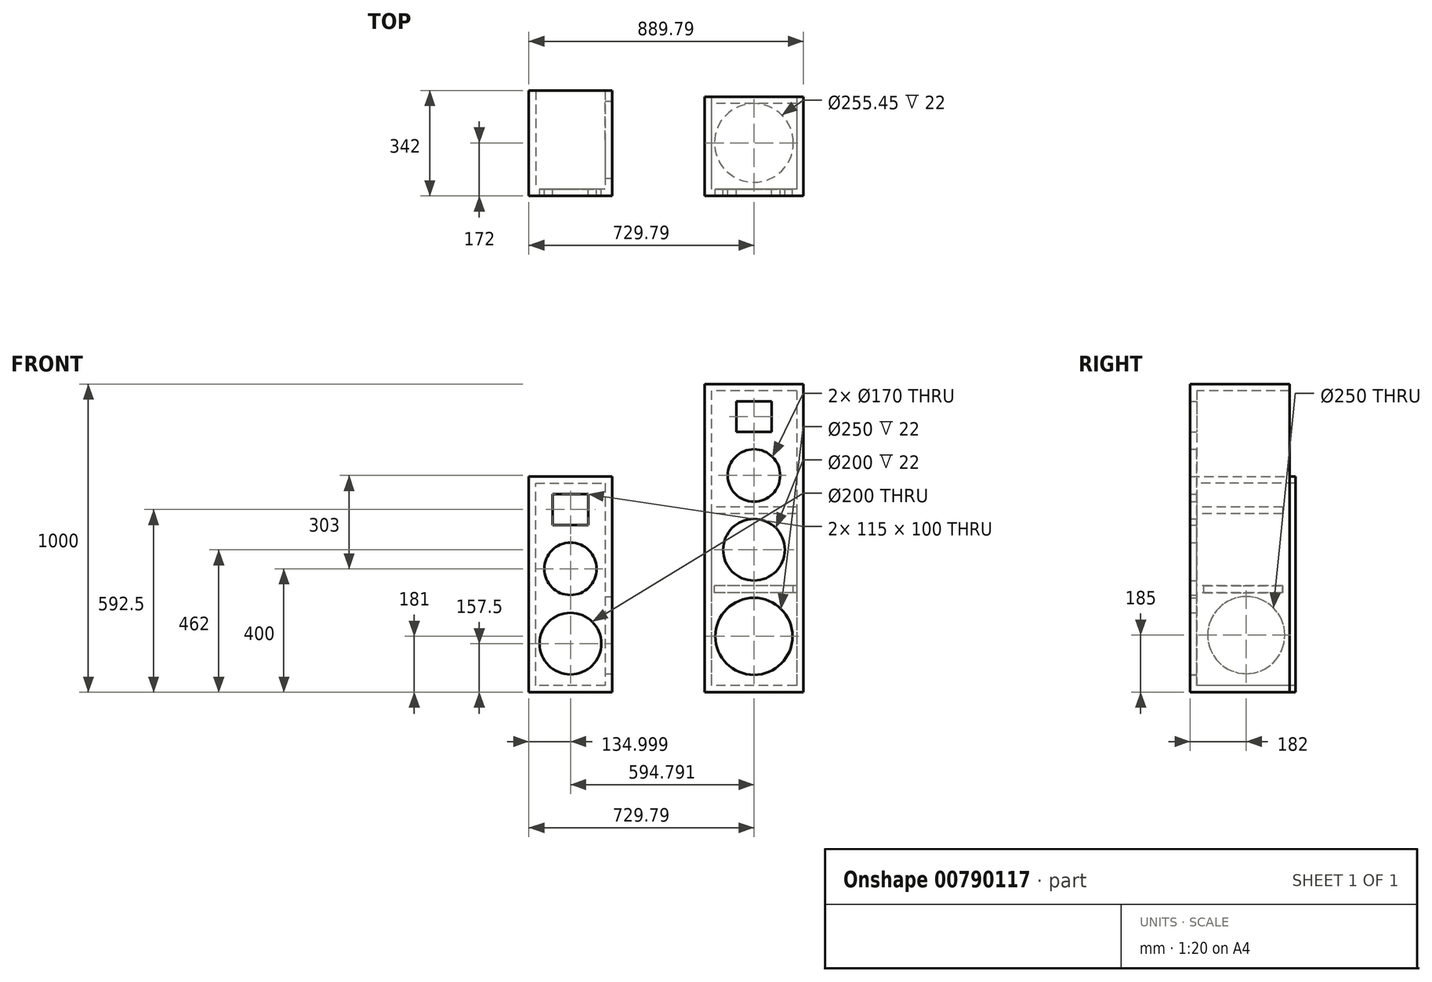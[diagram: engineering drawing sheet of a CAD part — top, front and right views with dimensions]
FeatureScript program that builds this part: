
annotation { "Feature Type Name" : "Feature", "Feature Type Description" : "" }
export const myFeature = defineFeature(function(context is Context, id is Id, definition is map)
    precondition{}
    {
        {
            var Q0;
            Q0=qCreatedBy(makeId("Front.planeOp"),FACE);
            var sketch = newSketch(context, id + "F0", { "sketchPlane" : qUnion([Q0])});
            skLineSegment(sketch, "E0.bottom", {"start": v(-160, 538) * mm, "end": v(160, 538) * mm});
            skLineSegment(sketch, "E0.top", {"start": v(-160, -462) * mm, "end": v(160, -462) * mm});
            skLineSegment(sketch, "E0.left", {"start": v(-160, 538) * mm, "end": v(-160, -462) * mm});
            skLineSegment(sketch, "E0.right", {"start": v(160, 538) * mm, "end": v(160, -462) * mm});
            skCircle(sketch, "E1", {"center": v(0, -281) * mm, "radius": 125 * mm});
            skCircle(sketch, "E2", {"center": v(0, 0) * mm, "radius": 100 * mm});
            skCircle(sketch, "E3", {"center": v(0, 241) * mm, "radius": 85 * mm});
            skLineSegment(sketch, "E4.bottom", {"start": v(-57.5, 482) * mm, "end": v(57.5, 482) * mm});
            skLineSegment(sketch, "E4.top", {"start": v(-57.5, 382) * mm, "end": v(57.5, 382) * mm});
            skLineSegment(sketch, "E4.left", {"start": v(-57.5, 482) * mm, "end": v(-57.5, 382) * mm});
            skLineSegment(sketch, "E4.right", {"start": v(57.5, 482) * mm, "end": v(57.5, 382) * mm});
            skLineSegment(sketch, "E5.bottom", {"start": v(-729.8, 238) * mm, "end": v(-459.8, 238) * mm});
            skLineSegment(sketch, "E5.top", {"start": v(-729.8, -462) * mm, "end": v(-459.8, -462) * mm});
            skLineSegment(sketch, "E5.left", {"start": v(-729.8, 238) * mm, "end": v(-729.8, -462) * mm});
            skLineSegment(sketch, "E5.right", {"start": v(-459.8, 238) * mm, "end": v(-459.8, -462) * mm});
            skCircle(sketch, "E6", {"center": v(-594.8, -304.5) * mm, "radius": 100 * mm});
            skCircle(sketch, "E7", {"center": v(-594.8, -62) * mm, "radius": 85 * mm});
            skPoint(sketch, "E8", {"position": v(0, 432) * mm});
            skLineSegment(sketch, "E9.bottom", {"start": v(-652.3, 180.5) * mm, "end": v(-537.3, 180.5) * mm});
            skLineSegment(sketch, "E9.top", {"start": v(-652.3, 80.5) * mm, "end": v(-537.3, 80.5) * mm});
            skLineSegment(sketch, "E9.left", {"start": v(-652.3, 180.5) * mm, "end": v(-652.3, 80.5) * mm});
            skLineSegment(sketch, "E9.right", {"start": v(-537.3, 180.5) * mm, "end": v(-537.3, 80.5) * mm});
            skSolve(sketch);
        }
        {
            var Q0;
            Q0 = qSketchRegion(id + "F0", true);
            extrude(context, id + "F1", {"entities" : qUnion([Q0]), "depth" : 22 * mm, "offsetDistance" : 25 * mm});
        }
        {
            var Q0;
            Q0=makeQuery(id+"F1.opExtrude","CAP_FACE",FACE,{"disambiguationData":[OSD([sQuery(id+"F0.wireOp",EDGE,"E0.bottom"),sQuery(id+"F0.wireOp",EDGE,"E0.top"),sQuery(id+"F0.wireOp",EDGE,"E0.left"),sQuery(id+"F0.wireOp",EDGE,"E0.right"),sQuery(id+"F0.wireOp",EDGE,"E1"),sQuery(id+"F0.wireOp",EDGE,"E2"),sQuery(id+"F0.wireOp",EDGE,"E3"),sQuery(id+"F0.wireOp",EDGE,"E4.bottom"),sQuery(id+"F0.wireOp",EDGE,"E4.top"),sQuery(id+"F0.wireOp",EDGE,"E4.left"),sQuery(id+"F0.wireOp",EDGE,"E4.right")])],"isStart":true});
            var sketch = newSketch(context, id + "F2", { "sketchPlane" : qUnion([Q0])});
            skLineSegment(sketch, "E10.bottom", {"start": v(-138, 516) * mm, "end": v(138, 516) * mm});
            skLineSegment(sketch, "E10.top", {"start": v(-138, -440) * mm, "end": v(138, -440) * mm});
            skLineSegment(sketch, "E10.left", {"start": v(-138, 516) * mm, "end": v(-138, -440) * mm});
            skLineSegment(sketch, "E10.right", {"start": v(138, 516) * mm, "end": v(138, -440) * mm});
            skSolve(sketch);
        }
        {
            var Q0;
            Q0=qCreatedBy(makeId("Front.planeOp"),FACE);
            var sketch = newSketch(context, id + "F3", { "sketchPlane" : qUnion([Q0])});
            skLineSegment(sketch, "E11.0", {"start": v(-707.8, -440) * mm, "end": v(-707.8, 216) * mm});
            skLineSegment(sketch, "E11.1", {"start": v(-481.8, -440) * mm, "end": v(-707.8, -440) * mm});
            skLineSegment(sketch, "E11.2", {"start": v(-481.8, 216) * mm, "end": v(-481.8, -440) * mm});
            skLineSegment(sketch, "E11.3", {"start": v(-707.8, 216) * mm, "end": v(-481.8, 216) * mm});
            skSolve(sketch);
        }
        {
            var Q0;
            Q0=makeQuery(id+"F1.opExtrude","CAP_FACE",FACE,{"disambiguationData":[OSD([sQuery(id+"F0.wireOp",EDGE,"E5.bottom"),sQuery(id+"F0.wireOp",EDGE,"E5.top"),sQuery(id+"F0.wireOp",EDGE,"E5.left"),sQuery(id+"F0.wireOp",EDGE,"E5.right"),sQuery(id+"F0.wireOp",EDGE,"E6"),sQuery(id+"F0.wireOp",EDGE,"E7"),sQuery(id+"F0.wireOp",EDGE,"ergSRJjx-bGEk-UiLp-R56Z-rpadYB1vBW9F.bottom"),sQuery(id+"F0.wireOp",EDGE,"ergSRJjx-bGEk-UiLp-R56Z-rpadYB1vBW9F.top"),sQuery(id+"F0.wireOp",EDGE,"ergSRJjx-bGEk-UiLp-R56Z-rpadYB1vBW9F.left"),sQuery(id+"F0.wireOp",EDGE,"ergSRJjx-bGEk-UiLp-R56Z-rpadYB1vBW9F.right")])],"isStart":true});
            extrude(context, id + "F4", {"entities" : qUnion([Q0]), "operationType" : NewBodyOperationType.ADD, "depth" : 320 * mm, "offsetDistance" : 25 * mm});
        }
        {
            var Q0;
            Q0=makeQuery(id+"F3.imprint","IMPRINT",FACE,{"disambiguationData":[TD([[makeQuery(id+"F3.imprint","IMPRINT",EDGE,{"derivedFrom":sQuery(id+"F3.wireOp",EDGE,"E11.0")}),-1.0]])]});
            extrude(context, id + "F5", {"entities" : qUnion([Q0]), "operationType" : NewBodyOperationType.REMOVE, "oppositeDirection" : true, "depth" : 824 * mm, "offsetDistance" : 25 * mm});
        }
        {
            var Q0;
            Q0=makeQuery(id+"F2.imprint","IMPRINT",FACE,{"disambiguationData":[TD([[makeQuery(id+"F2.imprint","IMPRINT",EDGE,{"derivedFrom":sQuery(id+"F2.wireOp",EDGE,"E10.bottom")}),1.0]])]});
            extrude(context, id + "F6", {"entities" : qUnion([Q0]), "operationType" : NewBodyOperationType.ADD, "depth" : 300 * mm, "offsetDistance" : 25 * mm});
        }
        {
            var Q0;
            {var subQ0=sQuery(id+"F0.wireOp",EDGE,"E5.right");Q0=makeQuery(id+"F4.boolean.opBoolean","MERGE",FACE,{"derivedFrom":[makeQuery(id+"F1.opExtrude","SWEPT_FACE",FACE,{"disambiguationData":[OSD([subQ0])]}),makeQuery(id+"F4.opExtrude","SWEPT_FACE",FACE,{"disambiguationData":[OSD([subQ0])]})]});}
            var sketch = newSketch(context, id + "F7", { "sketchPlane" : qUnion([Q0])});
            skCircle(sketch, "E12", {"center": v(160, -277) * mm, "radius": 125 * mm});
            skSolve(sketch);
        }
        {
            var Q0;
            Q0 = qSketchRegion(id + "F7", true);
            extrude(context, id + "F8", {"entities" : qUnion([Q0]), "operationType" : NewBodyOperationType.REMOVE, "oppositeDirection" : true, "depth" : 25 * mm, "offsetDistance" : 25 * mm});
        }
        {
            var Q0;
            Q0=makeQuery(id+"F1.opExtrude","CAP_FACE",FACE,{"disambiguationData":[OSD([sQuery(id+"F0.wireOp",EDGE,"E0.bottom"),sQuery(id+"F0.wireOp",EDGE,"E0.top"),sQuery(id+"F0.wireOp",EDGE,"E0.left"),sQuery(id+"F0.wireOp",EDGE,"E0.right"),sQuery(id+"F0.wireOp",EDGE,"E1"),sQuery(id+"F0.wireOp",EDGE,"E2"),sQuery(id+"F0.wireOp",EDGE,"E3"),sQuery(id+"F0.wireOp",EDGE,"E4.bottom"),sQuery(id+"F0.wireOp",EDGE,"E4.top"),sQuery(id+"F0.wireOp",EDGE,"E4.left"),sQuery(id+"F0.wireOp",EDGE,"E4.right")])],"isStart":true});
            var sketch = newSketch(context, id + "F9", { "sketchPlane" : qUnion([Q0])});
            skLineSegment(sketch, "E13.bottom", {"start": v(-138, -117) * mm, "end": v(138, -117) * mm});
            skLineSegment(sketch, "E13.top", {"start": v(-138, -139) * mm, "end": v(138, -139) * mm});
            skLineSegment(sketch, "E13.left", {"start": v(-138, -117) * mm, "end": v(-138, -139) * mm});
            skLineSegment(sketch, "E13.right", {"start": v(138, -117) * mm, "end": v(138, -139) * mm});
            skLineSegment(sketch, "E14.bottom", {"start": v(-138, 139) * mm, "end": v(138, 139) * mm});
            skLineSegment(sketch, "E14.top", {"start": v(-138, 117) * mm, "end": v(138, 117) * mm});
            skLineSegment(sketch, "E14.left", {"start": v(-138, 139) * mm, "end": v(-138, 117) * mm});
            skLineSegment(sketch, "E14.right", {"start": v(138, 139) * mm, "end": v(138, 117) * mm});
            skSolve(sketch);
        }
        {
            var Q0;
            Q0 = qSketchRegion(id + "F9", true);
            extrude(context, id + "F10", {"entities" : qUnion([Q0]), "operationType" : NewBodyOperationType.ADD, "depth" : 278 * mm, "offsetDistance" : 25 * mm});
        }
        {
            var Q0;
            Q0=makeQuery(id+"F10.opExtrude","SWEPT_FACE",FACE,{"disambiguationData":[OSD([sQuery(id+"F9.wireOp",EDGE,"E13.bottom")])]});
            var sketch = newSketch(context, id + "F11", { "sketchPlane" : qUnion([Q0])});
            skCircle(sketch, "E15", {"center": v(0, 150) * mm, "radius": 127.73 * mm});
            skSolve(sketch);
        }
        {
            var Q0;
            Q0 = qSketchRegion(id + "F11", true);
            extrude(context, id + "F12", {"entities" : qUnion([Q0]), "operationType" : NewBodyOperationType.REMOVE, "oppositeDirection" : true, "depth" : 25 * mm, "offsetDistance" : 25 * mm});
        }
    });
